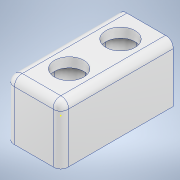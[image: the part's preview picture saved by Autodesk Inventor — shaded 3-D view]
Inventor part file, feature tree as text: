
AUTODESK INVENTOR PART (.ipt)
format: ipt  version: 2021 (Build 250183000, 183)  size: 1,302,016 bytes
history: native  units: in
note: dims shown in document units (in); Inventor stores cm internally (conversion verified against a paired STEP export)
features: extrude x8, other x6, sketch x3, fillet x2
ambient origin geometry x8: Origin, YZ Plane, XZ Plane, XY Plane, X Axis, Y Axis, Z Axis, Center Point
bodies: Body1 (feature_tree)
feature tree (19):
  extrude  "Base"  Depth=1.6535in
  extrude  "Top"  Depth=1.122in
  extrude  "Walls"  Depth=1.122in
  fillet  "Outer"  Radius=1.122in
  extrude  "Wire"  Depth=1.5748in
  extrude  "Wall Holes"  Depth=1.5748in
  extrude  "Text"  Depth=1.5748in
  sketch  "Sketch16"  dims[d6=6.8898in d7=1.6535in]
  extrude  "Extrusion9"  Depth=0.7087in TaperAngle=0.0deg
  extrude  "Extrusion10"  Depth=0.315in
  fillet  "Fillet8"  Radius=0.315in
  other  "Base Sketch"
  other  "Top Sketch"
  other  "Walls Sketch"
  other  "Wire Sketch"
  other  "Wall Holes Sketch"
  other  "Text Sketch"
  sketch  "Sketch17"  dims[d8=1.7717in d9=0.0in d10=1.122in]
  sketch  "Sketch18"  dims[d11=1.122in d12=1.122in d13=1.122in d14=1.5748in d15=1.5748in d16=1.5748in d19=0.7087in d20=0.0in d21=0.315in d22=0.315in d23=0.2362in d24=0.2362in d25=1.4764in d26=0.0in d27=0.8976in d28=0.8976in d29=0.8976in d30=0.8976in d31=0.7874in d32=3.4449in d33=1.1811in d35=1.0827in d36=0.2362in d38=0.3937in d39=0.0in d50=0.1575in d52=0.315in d55=0.1969in d56=0.0in d58=0.4528in d65=0.315in d66=0.1575in d67=0.1575in d68=0.315in d69=0.2774in d70=0.2774in d71=0.0499in d72=0.0499in d73=0.0787in d74=0.0in d77=0.6102in d78=0.6102in d79=0.0in d80=0.0in d81=0.5906in d82=0.0in d83=3.4449in d84=0.0in d85=0.4724in d86=0.1575in d87=0.1575in d88=0.8268in d89=0.315in d90=0.1575in d44=0.0197in d45=0.0344in d46=0.0197in d47=0.0344in d48=0.0197in d49=0.0344in d59=0.0197in d60=0.0344in d61=0.0197in d62=0.0344in]
